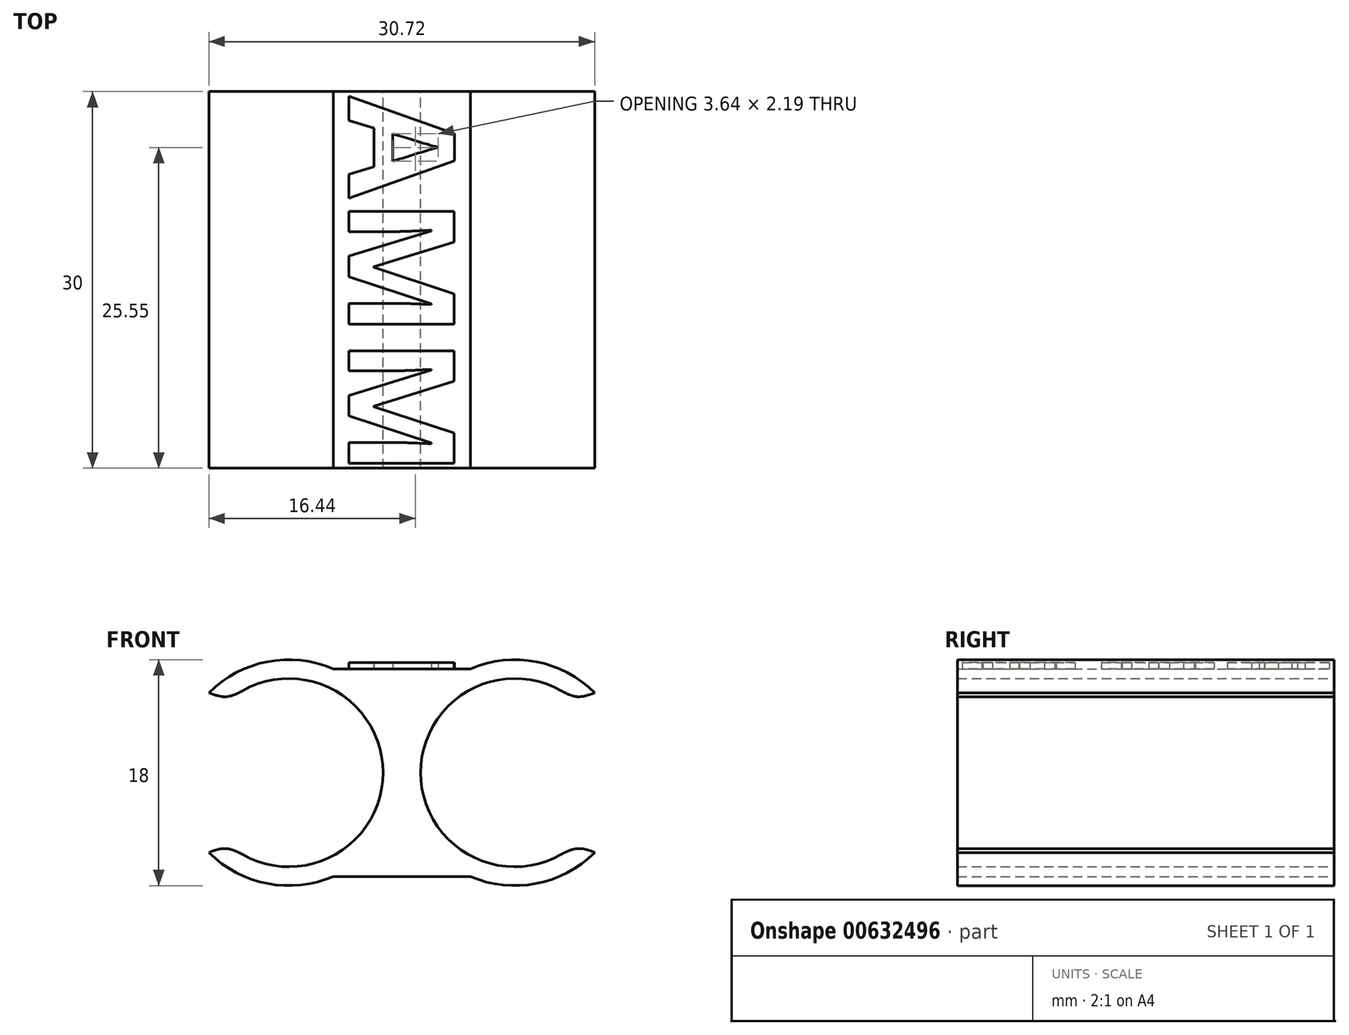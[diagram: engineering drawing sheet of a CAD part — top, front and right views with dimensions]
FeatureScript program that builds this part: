
annotation { "Feature Type Name" : "Feature", "Feature Type Description" : "" }
export const myFeature = defineFeature(function(context is Context, id is Id, definition is map)
    precondition{}
    {
        {
            var Q0;
            Q0=qCreatedBy(makeId("Front.planeOp"),FACE);
            var sketch = newSketch(context, id + "F0", { "sketchPlane" : qUnion([Q0])});
            skCircle(sketch, "E0", {"center": v(9, 0) * mm, "radius": 7.5 * mm});
            skCircle(sketch, "E1", {"center": v(-9, 0) * mm, "radius": 7.5 * mm});
            skCircle(sketch, "E2", {"center": v(9, 0) * mm, "radius": 9 * mm});
            skCircle(sketch, "E3", {"center": v(-9, 0) * mm, "radius": 9 * mm});
            skLineSegment(sketch, "E4", {"start": v(-5.46, 8.27) * mm, "end": v(5.46, 8.27) * mm});
            skLineSegment(sketch, "E5", {"start": v(5.46, -8.27) * mm, "end": v(-5.46, -8.27) * mm});
            skSolve(sketch);
        }
        {
            var Q0;
            Q0=makeQuery(id+"F0.imprint","IMPRINT",FACE,{"disambiguationData":[TD([[makeQuery(id+"F0.imprint","IMPRINT",EDGE,{"derivedFrom":sQuery(id+"F0.wireOp",EDGE,"E1")}),-1.0]])]});
            var Q1;
            {var subQ0=sQuery(id+"F0.wireOp",EDGE,"E4");Q1=makeQuery(id+"F0.imprint","IMPRINT",FACE,{"disambiguationData":[TD([[makeQuery(id+"F0.imprint","IMPRINT",EDGE,{"derivedFrom":subQ0}),-1.0]])]});}
            var Q2;
            Q2=makeQuery(id+"F0.imprint","IMPRINT",FACE,{"disambiguationData":[TD([[makeQuery(id+"F0.imprint","IMPRINT",EDGE,{"derivedFrom":sQuery(id+"F0.wireOp",EDGE,"E0")}),-1.0]])]});
            var Q3;
            {var subQ0=sQuery(id+"F0.wireOp",EDGE,"E5");Q3=makeQuery(id+"F0.imprint","IMPRINT",FACE,{"disambiguationData":[TD([[makeQuery(id+"F0.imprint","IMPRINT",EDGE,{"derivedFrom":subQ0}),-1.0]])]});}
            extrude(context, id + "F1", {"entities" : qUnion([Q0, Q1, Q2, Q3]), "depth" : 30 * mm, "offsetDistance" : 25 * mm});
        }
        {
            var Q0;
            Q0=qCreatedBy(makeId("Front.planeOp"),FACE);
            var sketch = newSketch(context, id + "F2", { "sketchPlane" : qUnion([Q0])});
            skLineSegment(sketch, "E6.bottom", {"start": v(-21.73, 0) * mm, "end": v(-15.36, -6.36) * mm});
            skLineSegment(sketch, "E6.top", {"start": v(-15.36, 6.36) * mm, "end": v(-9, 0) * mm});
            skLineSegment(sketch, "E6.left", {"start": v(-21.73, 0) * mm, "end": v(-15.36, 6.36) * mm});
            skLineSegment(sketch, "E6.right", {"start": v(-15.36, -6.36) * mm, "end": v(-9, 0) * mm});
            skPoint(sketch, "E6.middle", {"position": v(-16.72, 0) * mm});
            skLineSegment(sketch, "E7.bottom", {"start": v(9, 0) * mm, "end": v(15.36, -6.36) * mm});
            skLineSegment(sketch, "E7.top", {"start": v(15.36, 6.36) * mm, "end": v(21.73, 0) * mm});
            skLineSegment(sketch, "E7.left", {"start": v(9, 0) * mm, "end": v(15.36, 6.36) * mm});
            skLineSegment(sketch, "E7.right", {"start": v(15.36, -6.36) * mm, "end": v(21.73, 0) * mm});
            skPoint(sketch, "E7.middle", {"position": v(-10.6, 0.6) * mm});
            skSolve(sketch);
        }
        {
            var Q0;
            Q0=makeQuery(id+"F2.imprint","IMPRINT",FACE,{"disambiguationData":[TD([[makeQuery(id+"F2.imprint","IMPRINT",EDGE,{"derivedFrom":sQuery(id+"F2.wireOp",EDGE,"E6.bottom")}),1.0]])]});
            var Q1;
            Q1=makeQuery(id+"F2.imprint","IMPRINT",FACE,{"disambiguationData":[TD([[makeQuery(id+"F2.imprint","IMPRINT",EDGE,{"derivedFrom":sQuery(id+"F2.wireOp",EDGE,"E7.bottom")}),1.0]])]});
            extrude(context, id + "F3", {"entities" : qUnion([Q0, Q1]), "operationType" : NewBodyOperationType.REMOVE, "depth" : 55 * mm, "offsetDistance" : 25 * mm});
        }
        {
            var Q0;
            Q0=makeQuery(id+"F3.boolean.opBoolean","INTERSECT",EDGE,{"derivedFrom":[makeQuery(id+"F1.opExtrude","SWEPT_FACE",FACE,{"disambiguationData":[OSD([sQuery(id+"F0.wireOp",EDGE,"E0")])]}),makeQuery(id+"F3.opExtrude","SWEPT_FACE",FACE,{"disambiguationData":[OSD([sQuery(id+"F2.wireOp",EDGE,"E7.left")])]})]});
            var Q1;
            Q1=makeQuery(id+"F3.boolean.opBoolean","INTERSECT",EDGE,{"derivedFrom":[makeQuery(id+"F1.opExtrude","SWEPT_FACE",FACE,{"disambiguationData":[OSD([sQuery(id+"F0.wireOp",EDGE,"E0")])]}),makeQuery(id+"F3.opExtrude","SWEPT_FACE",FACE,{"disambiguationData":[OSD([sQuery(id+"F2.wireOp",EDGE,"E7.bottom")])]})]});
            var Q2;
            Q2=makeQuery(id+"F3.boolean.opBoolean","INTERSECT",EDGE,{"derivedFrom":[makeQuery(id+"F1.opExtrude","SWEPT_FACE",FACE,{"disambiguationData":[OSD([sQuery(id+"F0.wireOp",EDGE,"E1")])]}),makeQuery(id+"F3.opExtrude","SWEPT_FACE",FACE,{"disambiguationData":[OSD([sQuery(id+"F2.wireOp",EDGE,"E6.top")])]})]});
            var Q3;
            Q3=makeQuery(id+"F3.boolean.opBoolean","INTERSECT",EDGE,{"derivedFrom":[makeQuery(id+"F1.opExtrude","SWEPT_FACE",FACE,{"disambiguationData":[OSD([sQuery(id+"F0.wireOp",EDGE,"E1")])]}),makeQuery(id+"F3.opExtrude","SWEPT_FACE",FACE,{"disambiguationData":[OSD([sQuery(id+"F2.wireOp",EDGE,"E6.right")])]})]});
            fillet(context, id + "F4", {"entities" : qUnion([Q0, Q1, Q2, Q3]), "radius" : 3 * mm, "tangentPropagation" : true, "rho" : .6, "crossSection" : FilletCrossSection.CONIC, "allowEdgeOverflow" : false});
        }
        {
            var Q0;
            Q0=makeQuery(id+"F1.opExtrude","SWEPT_FACE",FACE,{"disambiguationData":[OSD([sQuery(id+"F0.wireOp",EDGE,"E4")])]});
            var sketch = newSketch(context, id + "F5", { "sketchPlane" : qUnion([Q0])});
            skText(sketch, "E8", { "text": "AMM", "fontName": "OpenSans-Bold.ttf"});
            const initialGuessF5  = {"E8": [-0.00423, -0.00038, 0, -1, 0.00847]};
            skSetInitialGuess(sketch, initialGuessF5);
            skSolve(sketch);
        }
        {
            var Q0;
            Q0 = qSketchRegion(id + "F5", true);
            extrude(context, id + "F6", {"entities" : qUnion([Q0]), "depth" : .5 * mm, "offsetDistance" : 25 * mm});
        }
    });
